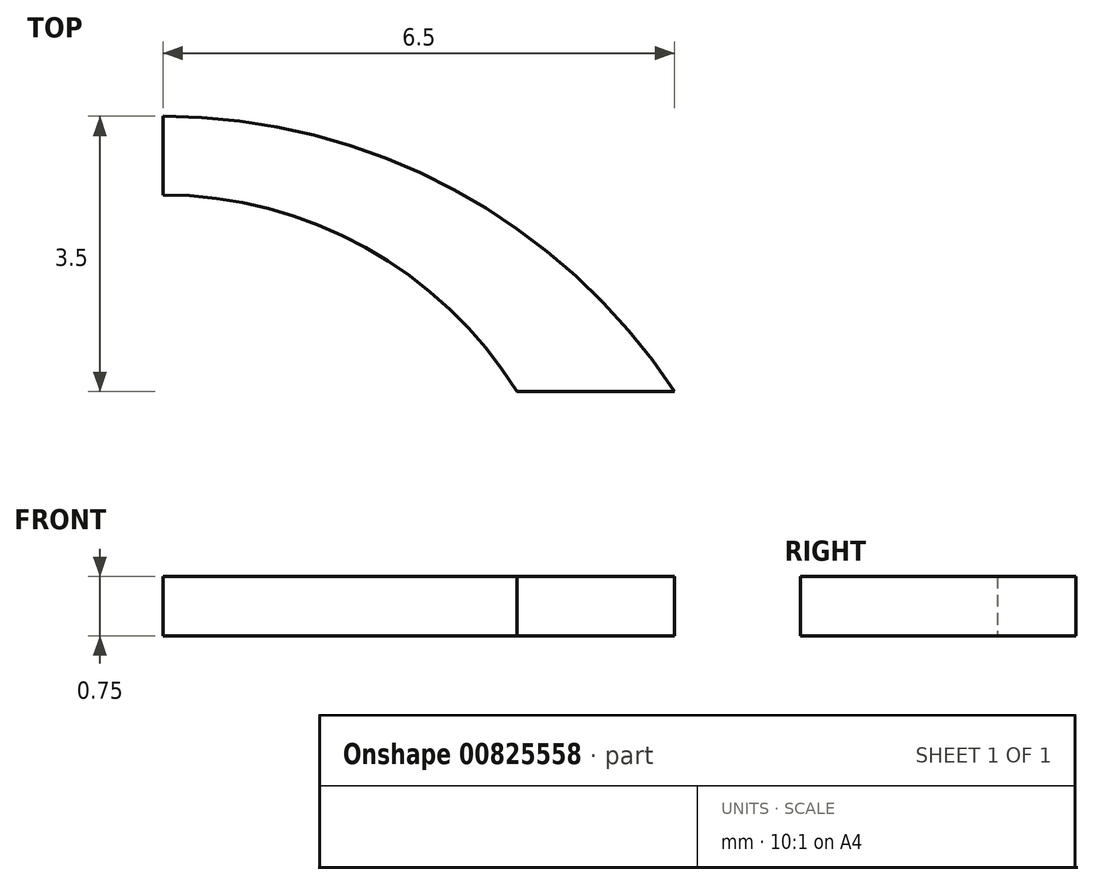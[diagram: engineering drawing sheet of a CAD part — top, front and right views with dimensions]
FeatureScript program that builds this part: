
annotation { "Feature Type Name" : "Feature", "Feature Type Description" : "" }
export const myFeature = defineFeature(function(context is Context, id is Id, definition is map)
    precondition{}
    {
        {
            var Q0;
            Q0=qCreatedBy(makeId("Top.planeOp"),FACE);
            var sketch = newSketch(context, id + "F0", { "sketchPlane" : qUnion([Q0])});
            skArc(sketch, "E0", {"start": v(4.5, 0) * mm, "mid": v(2.57, 1.83) * mm, "end": v(0, 2.5) * mm});
            skLineSegment(sketch, "E1", {"start": v(4.5, 0) * mm, "end": v(6.5, 0) * mm});
            skArc(sketch, "E2", {"start": v(6.5, 0) * mm, "mid": v(3.7, 2.57) * mm, "end": v(0, 3.5) * mm});
            skPoint(sketch, "E3", {"position": v(-6.5, 0) * mm});
            skPoint(sketch, "E4", {"position": v(0, 3.5) * mm});
            skPoint(sketch, "E5", {"position": v(0, 2.5) * mm});
            skPoint(sketch, "E6", {"position": v(-4.5, 0) * mm});
            skLineSegment(sketch, "E7", {"start": v(0, 3.5) * mm, "end": v(0, 2.5) * mm});
            skSolve(sketch);
        }
        {
            var Q0;
            Q0 = qSketchRegion(id + "F0", true);
            extrude(context, id + "F1", {"entities" : qUnion([Q0]), "depth" : 0.75 * mm, "offsetDistance" : 25 * mm});
        }
    });
